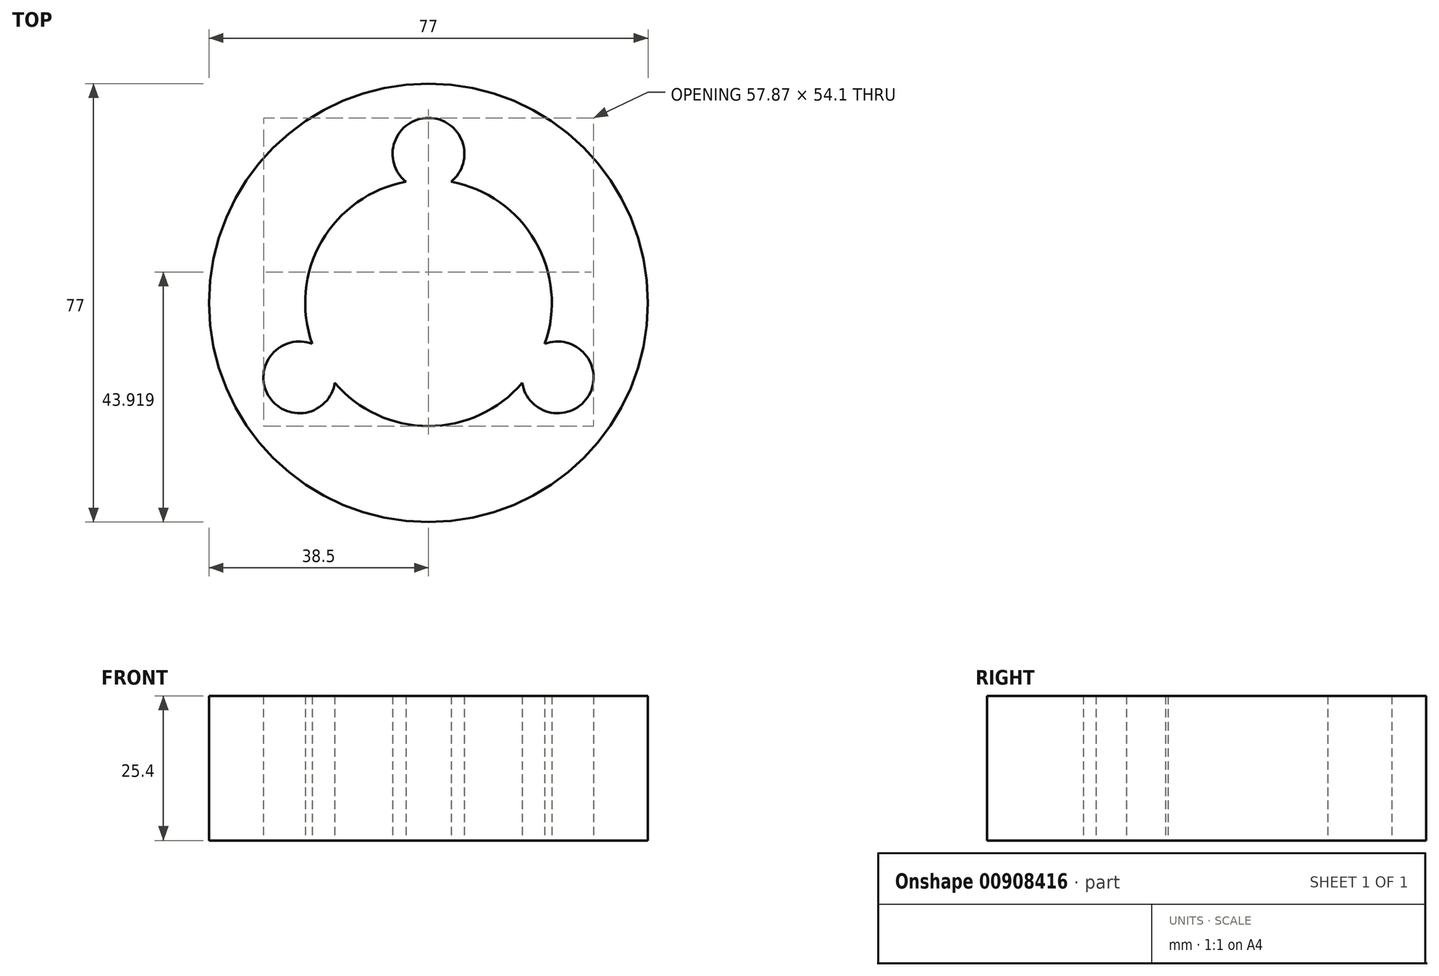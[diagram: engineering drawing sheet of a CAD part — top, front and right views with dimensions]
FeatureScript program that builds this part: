
annotation { "Feature Type Name" : "Feature", "Feature Type Description" : "" }
export const myFeature = defineFeature(function(context is Context, id is Id, definition is map)
    precondition{}
    {
        {
            var Q0;
            Q0=qCreatedBy(makeId("Top.planeOp"),FACE);
            var sketch = newSketch(context, id + "F0", { "sketchPlane" : qUnion([Q0])});
            skCircle(sketch, "E0", {"center": v(0, 0) * mm, "radius": 38.5 * mm});
            skCircle(sketch, "E1", {"center": v(0, 26.16) * mm, "radius": 6.3 * mm});
            skCircle(sketch, "E2.1.0", {"center": v(-22.66, -13.08) * mm, "radius": 6.3 * mm});
            skCircle(sketch, "E2.2.0", {"center": v(22.66, -13.08) * mm, "radius": 6.3 * mm});
            skCircle(sketch, "E3", {"center": v(0, 0) * mm, "radius": 21.63 * mm});
            skSolve(sketch);
        }
        {
            var Q0;
            Q0=makeQuery(id+"F0.imprint","IMPRINT",FACE,{"disambiguationData":[TD([[makeQuery(id+"F0.imprint","IMPRINT",EDGE,{"derivedFrom":sQuery(id+"F0.wireOp",EDGE,"E0")}),1.0]])]});
            extrude(context, id + "F1", {"entities" : qUnion([Q0]), "depth" : 25.4 * mm, "offsetDistance" : 25.4 * mm});
        }
    });
